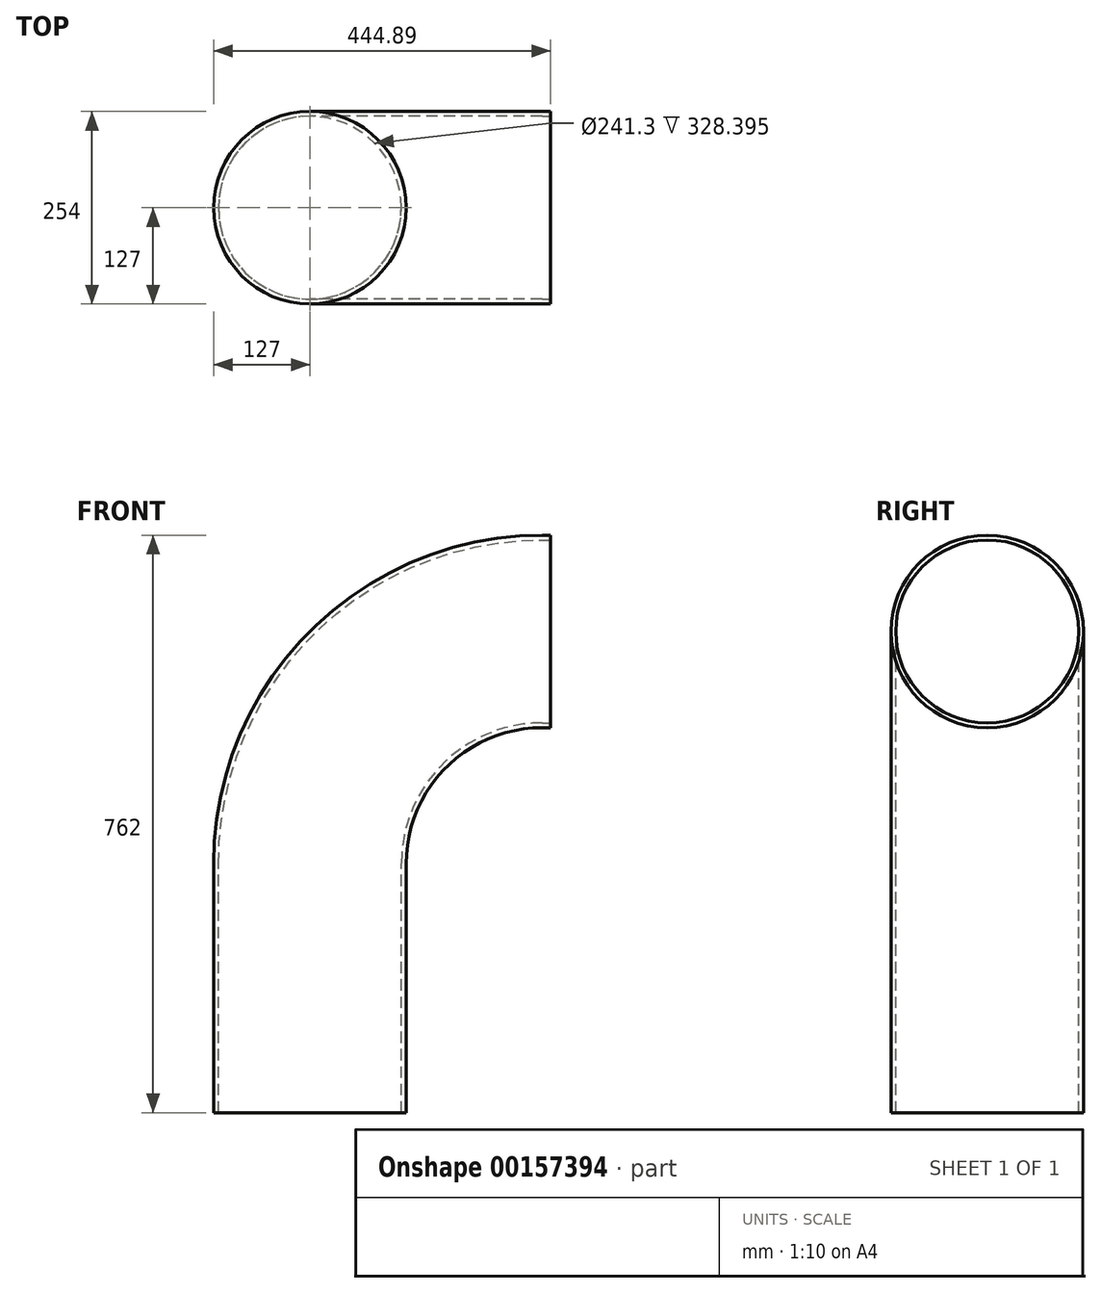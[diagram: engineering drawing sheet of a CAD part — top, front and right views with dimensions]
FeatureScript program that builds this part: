
annotation { "Feature Type Name" : "Feature", "Feature Type Description" : "" }
export const myFeature = defineFeature(function(context is Context, id is Id, definition is map)
    precondition{}
    {
        {
            var Q0;
            Q0=qCreatedBy(makeId("Front.planeOp"),FACE);
            var sketch = newSketch(context, id + "F0", { "sketchPlane" : qUnion([Q0])});
            skLineSegment(sketch, "E0.bottom", {"start": v(0, 0) * mm, "end": v(-254, 0) * mm});
            skLineSegment(sketch, "E0.left", {"start": v(0, 0) * mm, "end": v(0, 328.4) * mm});
            skLineSegment(sketch, "E0.right", {"start": v(-254, 0) * mm, "end": v(-254, 328.4) * mm});
            skLineSegment(sketch, "E1.bottom", {"start": v(179.6, 762) * mm, "end": v(508, 762) * mm});
            skLineSegment(sketch, "E1.top", {"start": v(179.6, 508) * mm, "end": v(508, 508) * mm});
            skLineSegment(sketch, "E1.right", {"start": v(508, 762) * mm, "end": v(508, 508) * mm});
            skArc(sketch, "E2", {"start": v(179.6, 508) * mm, "mid": v(52.6, 455.4) * mm, "end": v(0, 328.4) * mm});
            skArc(sketch, "E3", {"start": v(179.6, 762) * mm, "mid": v(-127, 635) * mm, "end": v(-254, 328.4) * mm});
            skSolve(sketch);
        }
        {
            var Q0;
            Q0 = qSketchRegion(id + "F0", true);
            extrude(context, id + "F1", {"entities" : qUnion([Q0]), "depth" : 254 * mm});
        }
        {
            var Q0;
            Q0=makeQuery(id+"F1.opExtrude","CAP_EDGE",EDGE,{"disambiguationData":[OSD([sQuery(id+"F0.wireOp",EDGE,"E1.top")])],"isStart":false});
            var Q1;
            Q1=makeQuery(id+"F1.opExtrude","CAP_EDGE",EDGE,{"disambiguationData":[OSD([sQuery(id+"F0.wireOp",EDGE,"E3")])],"isStart":false});
            var Q2;
            Q2=makeQuery(id+"F1.opExtrude","CAP_EDGE",EDGE,{"disambiguationData":[OSD([sQuery(id+"F0.wireOp",EDGE,"E3")])],"isStart":true});
            var Q3;
            Q3=makeQuery(id+"F1.opExtrude","CAP_EDGE",EDGE,{"disambiguationData":[OSD([sQuery(id+"F0.wireOp",EDGE,"E2")])],"isStart":true});
            fillet(context, id + "F2", {"entities" : qUnion([Q0, Q1, Q2, Q3]), "radius" : 127 * mm, "tangentPropagation" : true, "allowEdgeOverflow" : false});
        }
        {
            var Q0;
            Q0=makeQuery(id+"F1.opExtrude","SWEPT_FACE",FACE,{"disambiguationData":[OSD([sQuery(id+"F0.wireOp",EDGE,"E0.bottom")])]});
            var Q1;
            Q1=makeQuery(id+"F1.opExtrude","SWEPT_FACE",FACE,{"disambiguationData":[OSD([sQuery(id+"F0.wireOp",EDGE,"E1.right")])]});
            shell(context, id + "F3", {"entities" : qUnion([Q0, Q1]), "thickness" : 6.35 * mm});
        }
        {
            var Q0;
            Q0=makeQuery(id+"F1.opExtrude","SWEPT_FACE",FACE,{"disambiguationData":[OSD([sQuery(id+"F0.wireOp",EDGE,"E1.right")])]});
            extrude(context, id + "F4", {"entities" : qUnion([Q0]), "operationType" : NewBodyOperationType.REMOVE, "oppositeDirection" : true, "depth" : 317.1 * mm});
        }
    });
